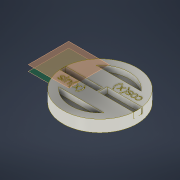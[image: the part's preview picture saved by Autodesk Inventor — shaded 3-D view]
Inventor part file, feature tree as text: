
AUTODESK INVENTOR PART (.ipt)
format: ipt  version: 2022 (Build 260153000, 153)  size: 949,760 bytes
history: native  units: in
note: dims shown in document units (in); Inventor stores cm internally (conversion verified against a paired STEP export)
features: sketch x4, extrude x4, plane x3
ambient origin geometry x8: Origin, YZ Plane, XZ Plane, XY Plane, X Axis, Y Axis, Z Axis, Center Point
bodies: Solid1 (feature_tree)
feature tree (11):
  sketch  "Sketch1"  dims[d1=0.75in d5=0.125in d6=0.0in]
  extrude  "Extrusion5"  Depth=0.125in TaperAngle=0.0deg
  plane  "Work Plane2"
  extrude  "Extrusion2"  Depth=0.0312in
  plane  "Work Plane3"
  plane  "Work Plane1"
  extrude  "Extrusion4"  Depth=0.4in
  extrude  "Extrusion3"  Depth=0.125in
  sketch  "Sketch2"  dims[d7=0.0312in d8=0.0in d9=1.25in]
  sketch  "Sketch3"  dims[d10=0.4in d11=0.4in]
  sketch  "Sketch4"  dims[d12=0.125in d13=0.0in d15=0.125in d16=0.125in d17=0.0in]
